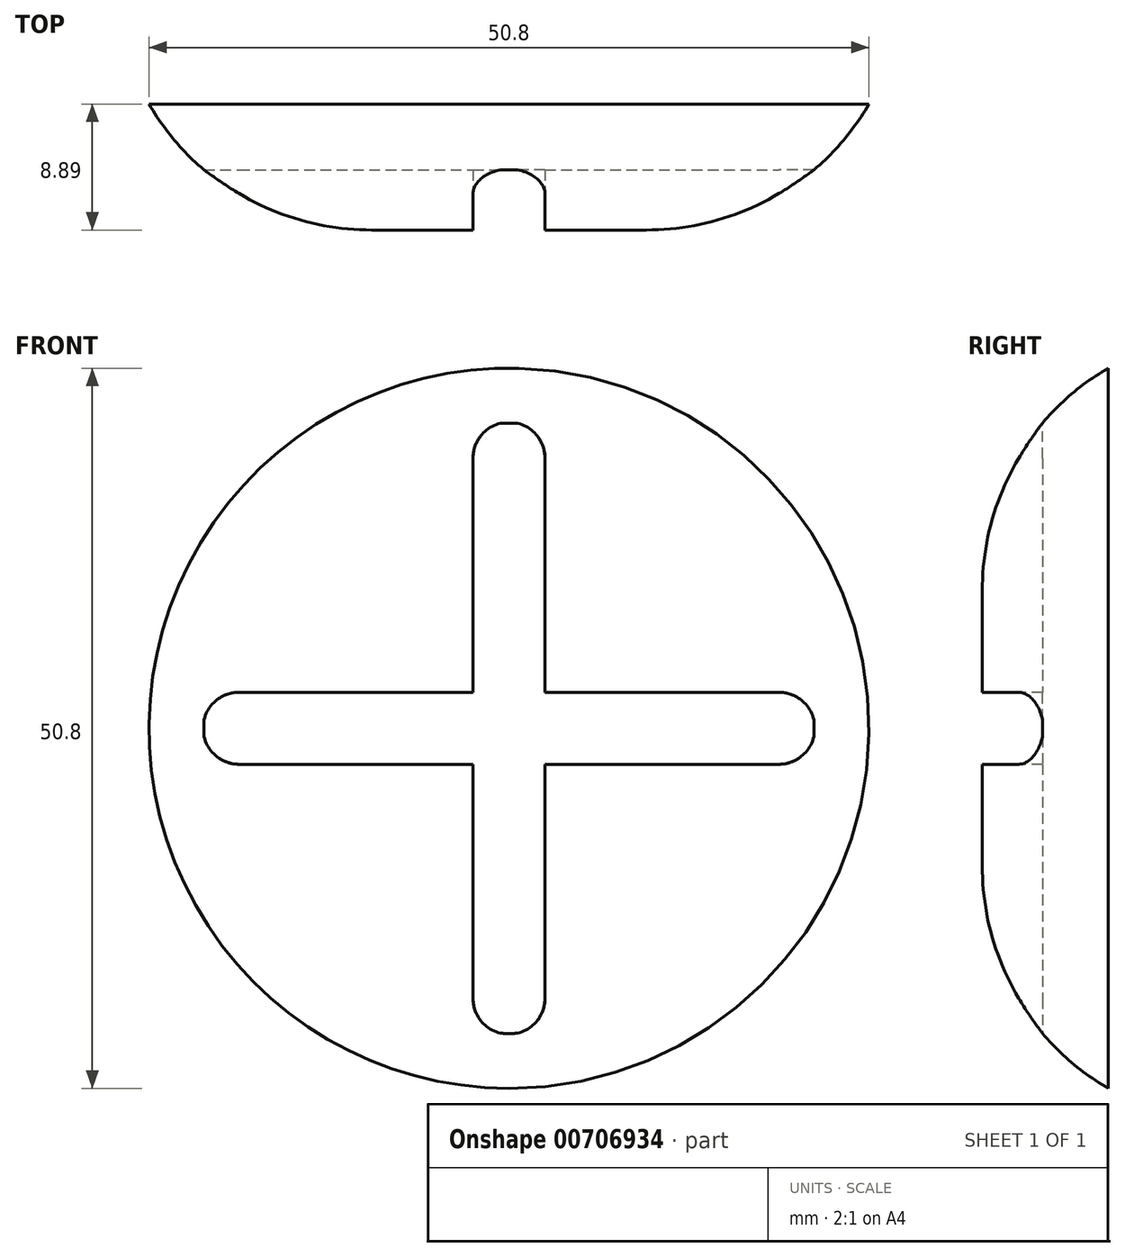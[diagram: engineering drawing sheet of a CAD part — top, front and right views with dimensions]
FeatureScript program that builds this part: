
annotation { "Feature Type Name" : "Feature", "Feature Type Description" : "" }
export const myFeature = defineFeature(function(context is Context, id is Id, definition is map)
    precondition{}
    {
        {
            var Q0;
            Q0=qCreatedBy(makeId("Front.planeOp"),FACE);
            var sketch = newSketch(context, id + "F0", { "sketchPlane" : qUnion([Q0])});
            skCircle(sketch, "E0", {"center": v(0, 0) * mm, "radius": 25.4 * mm});
            skSolve(sketch);
        }
        {
            var Q0;
            Q0=makeQuery(id+"F0.imprint","IMPRINT",FACE,{"disambiguationData":[TD([[makeQuery(id+"F0.imprint","IMPRINT",EDGE,{"derivedFrom":sQuery(id+"F0.wireOp",EDGE,"E0")}),1.0]])]});
            extrude(context, id + "F1", {"entities" : qUnion([Q0]), "depth" : 8.9 * mm, "offsetDistance" : 25.4 * mm});
        }
        {
            var Q0;
            Q0=makeQuery(id+"F1.opExtrude","CAP_EDGE",EDGE,{"disambiguationData":[OSD([sQuery(id+"F0.wireOp",EDGE,"E0")])],"isStart":false});
            fillet(context, id + "F2", {"entities" : qUnion([Q0]), "radius" : 17.78 * mm, "tangentPropagation" : true, "allowEdgeOverflow" : false});
        }
        {
            var Q0;
            Q0=makeQuery(id+"F1.opExtrude","CAP_FACE",FACE,{"disambiguationData":[OSD([sQuery(id+"F0.wireOp",EDGE,"E0")])],"isStart":false});
            var sketch = newSketch(context, id + "F3", { "sketchPlane" : qUnion([Q0])});
            skLineSegment(sketch, "E1.bottom", {"start": v(-2.54, 19.05) * mm, "end": v(2.54, 19.05) * mm});
            skLineSegment(sketch, "E1.top", {"start": v(-2.54, -19.05) * mm, "end": v(2.54, -19.05) * mm});
            skLineSegment(sketch, "E1.left", {"start": v(-2.54, 19.05) * mm, "end": v(-2.54, -19.05) * mm});
            skLineSegment(sketch, "E1.right", {"start": v(2.54, 19.05) * mm, "end": v(2.54, -19.05) * mm});
            skLineSegment(sketch, "E2.bottom", {"start": v(-19.05, 2.54) * mm, "end": v(19.05, 2.54) * mm});
            skLineSegment(sketch, "E2.top", {"start": v(-19.05, -2.54) * mm, "end": v(19.05, -2.54) * mm});
            skLineSegment(sketch, "E2.left", {"start": v(-19.05, 2.54) * mm, "end": v(-19.05, -2.54) * mm});
            skLineSegment(sketch, "E2.right", {"start": v(19.05, 2.54) * mm, "end": v(19.05, -2.54) * mm});
            skArc(sketch, "E3", {"start": v(-19.05, 2.54) * mm, "mid": v(-21.59, 0) * mm, "end": v(-19.05, -2.54) * mm});
            skArc(sketch, "E4", {"start": v(19.05, -2.54) * mm, "mid": v(21.6, 0) * mm, "end": v(19.05, 2.54) * mm});
            skArc(sketch, "E5", {"start": v(2.54, 19.05) * mm, "mid": v(0, 21.59) * mm, "end": v(-2.54, 19.05) * mm});
            skArc(sketch, "E6", {"start": v(-2.54, -19.05) * mm, "mid": v(0, -21.59) * mm, "end": v(2.54, -19.05) * mm});
            skSolve(sketch);
        }
        {
            var Q0;
            {var subQ0=sQuery(id+"F3.wireOp",EDGE,"E1.bottom");Q0=makeQuery(id+"F3.imprint","IMPRINT",FACE,{"disambiguationData":[TD([[makeQuery(id+"F3.imprint","IMPRINT",EDGE,{"derivedFrom":subQ0}),-1.0]])]});}
            var Q1;
            Q1=makeQuery(id+"F3.imprint","IMPRINT",FACE,{"disambiguationData":[TD([[makeQuery(id+"F3.imprint","IMPRINT",EDGE,{"derivedFrom":sQuery(id+"F3.wireOp",EDGE,"E1.bottom")}),1.0]])]});
            var Q2;
            {var subQ0=sQuery(id+"F3.wireOp",EDGE,"E2.bottom");var subQ1=sQuery(id+"F3.wireOp",EDGE,"E1.left");var subQ2=makeQuery(id+"F3.imprint","INTERSECT",VERTEX,{"derivedFrom":[subQ1,subQ0]});Q2=makeQuery(id+"F3.imprint","IMPRINT",FACE,{"disambiguationData":[TD([[makeQuery(id+"F3.imprint","IMPRINT",EDGE,{"disambiguationData":[TD([[subQ2,-1.0]])],"derivedFrom":subQ0}),1.0]])]});}
            var Q3;
            {var subQ0=sQuery(id+"F3.wireOp",EDGE,"E2.bottom");var subQ1=sQuery(id+"F3.wireOp",EDGE,"E1.left");var subQ2=makeQuery(id+"F3.imprint","INTERSECT",VERTEX,{"derivedFrom":[subQ1,subQ0]});Q3=makeQuery(id+"F3.imprint","IMPRINT",FACE,{"disambiguationData":[TD([[makeQuery(id+"F3.imprint","IMPRINT",EDGE,{"disambiguationData":[TD([[subQ2,-1.0]])],"derivedFrom":subQ1}),1.0]])]});}
            var Q4;
            {var subQ0=sQuery(id+"F3.wireOp",EDGE,"E2.top");var subQ1=sQuery(id+"F3.wireOp",EDGE,"E1.left");var subQ2=makeQuery(id+"F3.imprint","INTERSECT",VERTEX,{"derivedFrom":[subQ1,subQ0]});Q4=makeQuery(id+"F3.imprint","IMPRINT",FACE,{"disambiguationData":[TD([[makeQuery(id+"F3.imprint","IMPRINT",EDGE,{"disambiguationData":[TD([[subQ2,-1.0]])],"derivedFrom":subQ0}),-1.0]])]});}
            var Q5;
            Q5=makeQuery(id+"F3.imprint","IMPRINT",FACE,{"disambiguationData":[TD([[makeQuery(id+"F3.imprint","IMPRINT",EDGE,{"derivedFrom":sQuery(id+"F3.wireOp",EDGE,"E1.top")}),-1.0]])]});
            var Q6;
            {var subQ0=sQuery(id+"F3.wireOp",EDGE,"E1.top");Q6=makeQuery(id+"F3.imprint","IMPRINT",FACE,{"disambiguationData":[TD([[makeQuery(id+"F3.imprint","IMPRINT",EDGE,{"derivedFrom":subQ0}),1.0]])]});}
            var Q7;
            {var subQ0=sQuery(id+"F3.wireOp",EDGE,"E2.bottom");var subQ1=sQuery(id+"F3.wireOp",EDGE,"E1.right");var subQ2=makeQuery(id+"F3.imprint","INTERSECT",VERTEX,{"derivedFrom":[subQ1,subQ0]});Q7=makeQuery(id+"F3.imprint","IMPRINT",FACE,{"disambiguationData":[TD([[makeQuery(id+"F3.imprint","IMPRINT",EDGE,{"disambiguationData":[TD([[subQ2,-1.0]])],"derivedFrom":subQ1}),1.0]])]});}
            var Q8;
            {var subQ1=sQuery(id+"F3.wireOp",EDGE,"E2.right");Q8=makeQuery(id+"F3.imprint","IMPRINT",FACE,{"disambiguationData":[TD([[makeQuery(id+"F3.imprint","IMPRINT",EDGE,{"derivedFrom":subQ1}),-1.0]])]});}
            var Q9;
            Q9=makeQuery(id+"F3.imprint","IMPRINT",FACE,{"disambiguationData":[TD([[makeQuery(id+"F3.imprint","IMPRINT",EDGE,{"derivedFrom":sQuery(id+"F3.wireOp",EDGE,"E2.right")}),1.0]])]});
            var Q10;
            {var subQ0=sQuery(id+"F3.wireOp",EDGE,"E2.bottom");var subQ1=sQuery(id+"F3.wireOp",EDGE,"E1.left");var subQ2=makeQuery(id+"F3.imprint","INTERSECT",VERTEX,{"derivedFrom":[subQ1,subQ0]});Q10=makeQuery(id+"F3.imprint","IMPRINT",FACE,{"disambiguationData":[TD([[makeQuery(id+"F3.imprint","IMPRINT",EDGE,{"disambiguationData":[TD([[subQ2,-1.0]])],"derivedFrom":subQ1}),-1.0]])]});}
            var Q11;
            {var subQ1=sQuery(id+"F3.wireOp",EDGE,"E2.left");Q11=makeQuery(id+"F3.imprint","IMPRINT",FACE,{"disambiguationData":[TD([[makeQuery(id+"F3.imprint","IMPRINT",EDGE,{"derivedFrom":subQ1}),1.0]])]});}
            var Q12;
            Q12=makeQuery(id+"F3.imprint","IMPRINT",FACE,{"disambiguationData":[TD([[makeQuery(id+"F3.imprint","IMPRINT",EDGE,{"derivedFrom":sQuery(id+"F3.wireOp",EDGE,"E2.left")}),-1.0]])]});
            extrude(context, id + "F4", {"entities" : qUnion([Q0, Q1, Q2, Q3, Q4, Q5, Q6, Q7, Q8, Q9, Q10, Q11, Q12]), "operationType" : NewBodyOperationType.REMOVE, "oppositeDirection" : true, "depth" : 4.24 * mm, "offsetDistance" : 25.4 * mm});
        }
    });
